# Revit family: QF_TRUE_GDM-35-HC~TSL01
name_source: partatom
category: Specialty Equipment
revit_build: Autodesk Revit 2016 (Build: 20150714_1515(x64)
units: mm (PartAtom-declared; Revit-internal decimal feet)

## family parameters
Always vertical = Yes
Cut with Voids When Loaded = No
Part Type = Normal
Room Calculation Point = No
Round Connector Dimension = Use Diameter
Shared = No
Work Plane-Based = No

## types (1)
- QF_TRUE_GDM-35-HC~TSL01
    Apparent Power = 748 VA
    Conn Conduit = Yes
    Conn Plug = NEMA 5-15P
    Cycle = 60 Hz
    Depth = 29 7/8"
    Description = SWING DOOR REFRIGERATOR WITH HYDROCARBON REFRIGERANT~TRUE STANDARD LOOK VERSION 01
    Elec Conn Connection Height = 0"
    Elec Conn RI Height = 0"
    FL Amps = 7 A
    Foodservice Equipment Identifier = Yes
    HP = 1/2
    Identify Quantity as Lot = Yes
    Length = 39 1/2"
    Manufacturer = TRUE
    Materials and Finishes = QF_Plastic - Black - Smooth
    Max Overcurrent Protection = 0 A
    Min Ckt Ampacity = 0 A
    Model = GDM-35-HC~TSL01
    Number of Poles = 1
    Phase = 1
    Volts = 115 V
    Watts = 748 W
    Weight in Pounds = 370

## geometry (parser evidence)
native form markers: Blend x12, Sweep x13
no freeform markers — native parametric forms only
